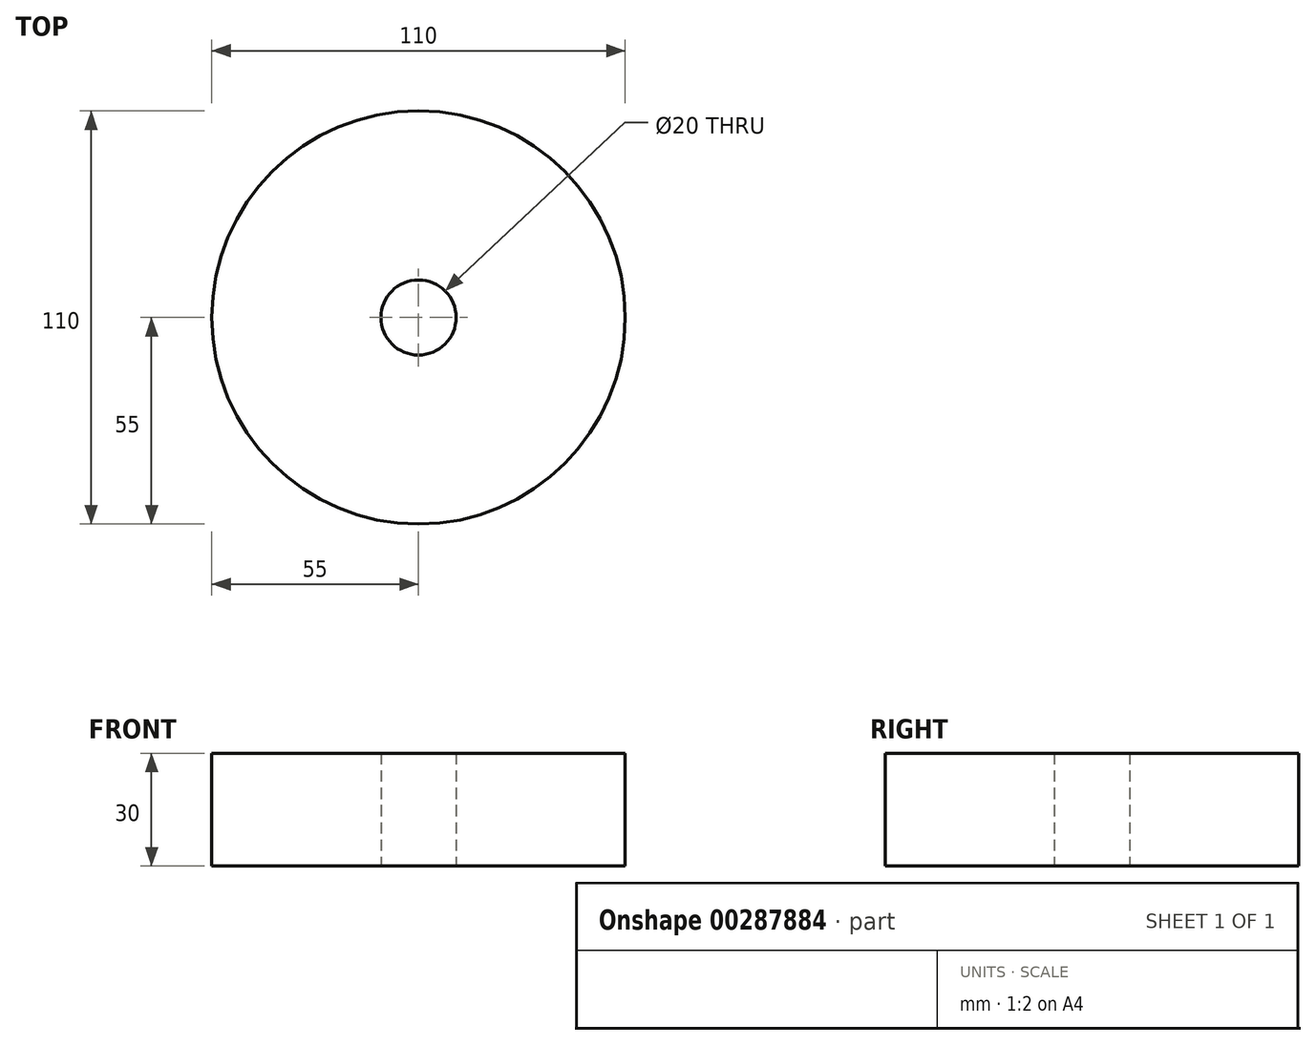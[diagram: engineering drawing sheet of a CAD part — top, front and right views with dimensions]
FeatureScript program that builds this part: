
annotation { "Feature Type Name" : "Feature", "Feature Type Description" : "" }
export const myFeature = defineFeature(function(context is Context, id is Id, definition is map)
    precondition{}
    {
        {
            var Q0;
            Q0=qCreatedBy(makeId("Top.planeOp"),FACE);
            var sketch = newSketch(context, id + "F0", { "sketchPlane" : qUnion([Q0])});
            skCircle(sketch, "E0", {"center": v(0, 0) * mm, "radius": 55 * mm});
            skCircle(sketch, "E1", {"center": v(0, 0) * mm, "radius": 10 * mm});
            skSolve(sketch);
        }
        {
            var Q0;
            Q0 = qSketchRegion(id + "F0", true);
            extrude(context, id + "F1", {"entities" : qUnion([Q0]), "depth" : 30 * mm});
        }
    });
